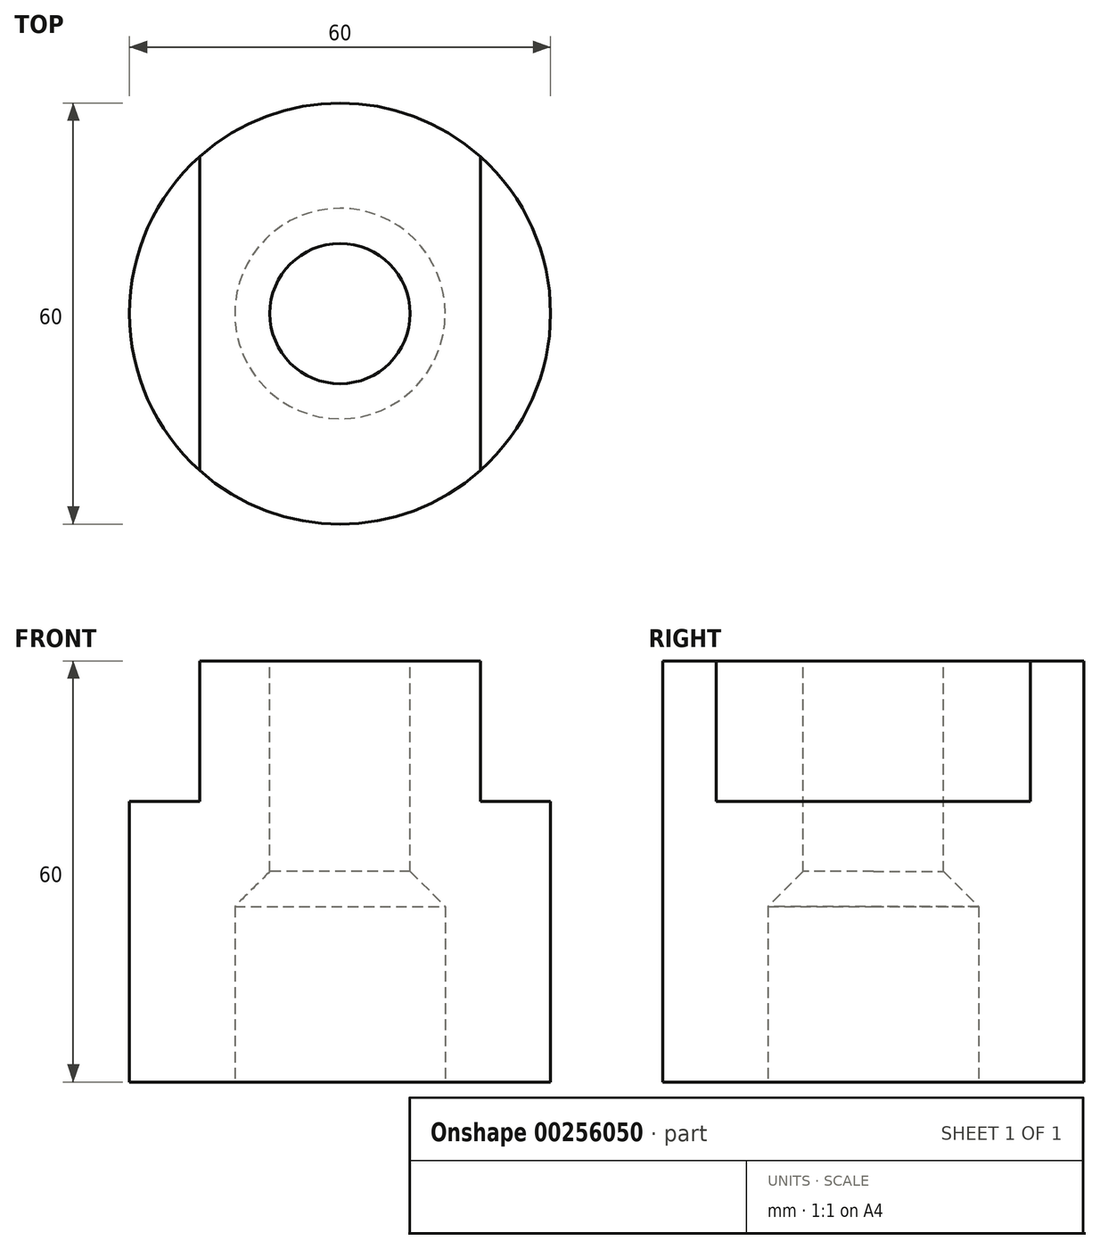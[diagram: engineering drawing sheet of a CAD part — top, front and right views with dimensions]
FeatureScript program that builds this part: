
annotation { "Feature Type Name" : "Feature", "Feature Type Description" : "" }
export const myFeature = defineFeature(function(context is Context, id is Id, definition is map)
    precondition{}
    {
        {
            var Q0;
            Q0=qCreatedBy(makeId("Top.planeOp"),FACE);
            var sketch = newSketch(context, id + "F0", { "sketchPlane" : qUnion([Q0])});
            skCircle(sketch, "E0", {"center": v(0, 0) * mm, "radius": 30 * mm});
            skSolve(sketch);
        }
        {
            var Q0;
            Q0 = qSketchRegion(id + "F0", true);
            extrude(context, id + "F1", {"entities" : qUnion([Q0]), "depth" : 60 * mm});
        }
        {
            var Q0;
            Q0=qCreatedBy(makeId("Front.planeOp"),FACE);
            var sketch = newSketch(context, id + "F2", { "sketchPlane" : qUnion([Q0])});
            skLineSegment(sketch, "E1.bottom", {"start": v(-30, 60) * mm, "end": v(-20, 60) * mm});
            skLineSegment(sketch, "E1.top", {"start": v(-30, 40) * mm, "end": v(-20, 40) * mm});
            skLineSegment(sketch, "E1.left", {"start": v(-30, 60) * mm, "end": v(-30, 40) * mm});
            skLineSegment(sketch, "E1.right", {"start": v(-20, 60) * mm, "end": v(-20, 40) * mm});
            skLineSegment(sketch, "E2.MirrorCS", {"start": v(30, 60) * mm, "end": v(20, 60) * mm});
            skLineSegment(sketch, "E3.MirrorCS", {"start": v(20, 60) * mm, "end": v(20, 40) * mm});
            skLineSegment(sketch, "E4.MirrorCS", {"start": v(30, 40) * mm, "end": v(20, 40) * mm});
            skLineSegment(sketch, "E5.MirrorCS", {"start": v(30, 60) * mm, "end": v(30, 40) * mm});
            skSolve(sketch);
        }
        {
            var Q0;
            Q0 = qSketchRegion(id + "F2", true);
            extrude(context, id + "F3", {"entities" : qUnion([Q0]), "operationType" : NewBodyOperationType.REMOVE, "endBound" : BoundingType.SYMMETRIC, "oppositeDirection" : true, "depth" : 100 * mm});
        }
        {
            var Q0;
            Q0=makeQuery(id+"F1.opExtrude","CAP_FACE",FACE,{"disambiguationData":[OSD([sQuery(id+"F0.wireOp",EDGE,"E0")])],"isStart":true});
            var sketch = newSketch(context, id + "F4", { "sketchPlane" : qUnion([Q0])});
            skCircle(sketch, "E6", {"center": v(0, 0) * mm, "radius": 15 * mm});
            skSolve(sketch);
        }
        {
            var Q0;
            Q0 = qSketchRegion(id + "F4", true);
            extrude(context, id + "F5", {"entities" : qUnion([Q0]), "operationType" : NewBodyOperationType.REMOVE, "oppositeDirection" : true, "depth" : 25 * mm});
        }
        {
            var Q0;
            Q0=makeQuery(id+"F1.opExtrude","CAP_FACE",FACE,{"disambiguationData":[OSD([sQuery(id+"F0.wireOp",EDGE,"E0")])],"isStart":false});
            var sketch = newSketch(context, id + "F6", { "sketchPlane" : qUnion([Q0])});
            skCircle(sketch, "E7", {"center": v(0, 0) * mm, "radius": 10 * mm});
            skSolve(sketch);
        }
        {
            var Q0;
            Q0 = qSketchRegion(id + "F6", true);
            extrude(context, id + "F7", {"entities" : qUnion([Q0]), "operationType" : NewBodyOperationType.REMOVE, "oppositeDirection" : true, "depth" : 100 * mm});
        }
        {
            var Q0;
            Q0=makeQuery(id+"F7.boolean.opBoolean","INTERSECT",EDGE,{"derivedFrom":[makeQuery(id+"F5.boolean.opBoolean","COPY",FACE,{"derivedFrom":makeQuery(id+"F5.opExtrude","CAP_FACE",FACE,{"disambiguationData":[OSD([sQuery(id+"F4.wireOp",EDGE,"E6")])],"isStart":false})}),makeQuery(id+"F7.opExtrude","SWEPT_FACE",FACE,{"disambiguationData":[OSD([sQuery(id+"F6.wireOp",EDGE,"E7")])]})]});
            chamfer(context, id + "F8", {"entities" : qUnion([Q0]), "width" : 5 * mm, "tangentPropagation" : true});
        }
    });
